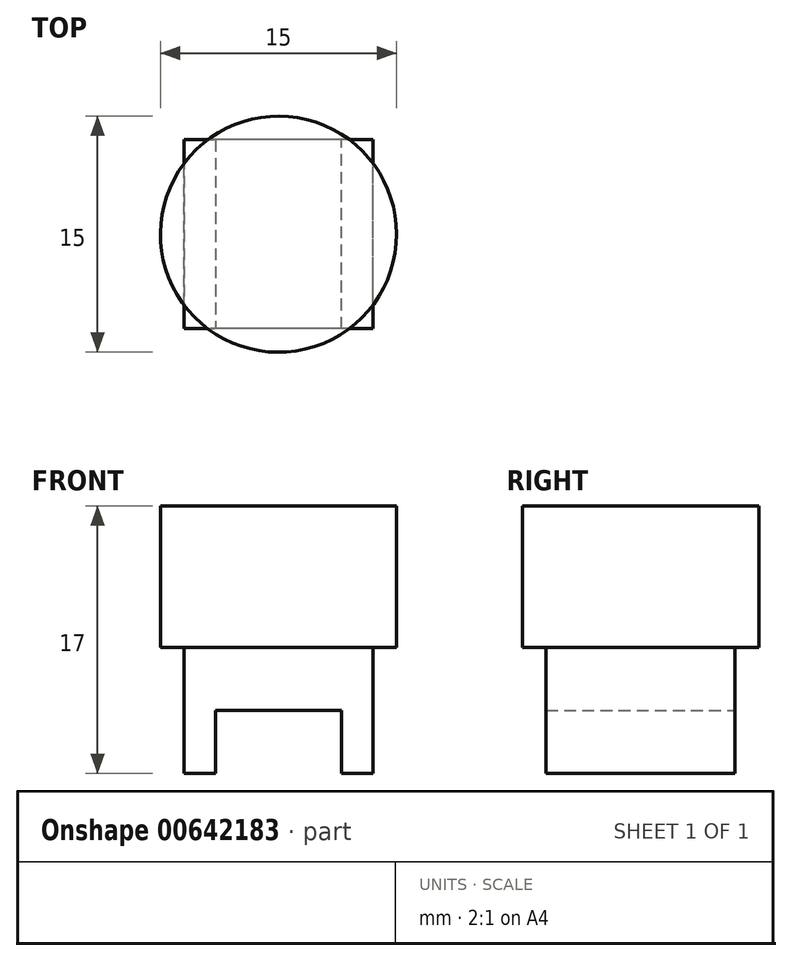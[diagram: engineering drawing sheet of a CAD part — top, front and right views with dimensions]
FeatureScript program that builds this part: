
annotation { "Feature Type Name" : "Feature", "Feature Type Description" : "" }
export const myFeature = defineFeature(function(context is Context, id is Id, definition is map)
    precondition{}
    {
        {
            var Q0;
            Q0=qCreatedBy(makeId("Top.planeOp"),FACE);
            var sketch = newSketch(context, id + "F0", { "sketchPlane" : qUnion([Q0])});
            skLineSegment(sketch, "E0.bottom", {"start": v(6, -6) * mm, "end": v(-6, -6) * mm});
            skLineSegment(sketch, "E0.top", {"start": v(6, 6) * mm, "end": v(-6, 6) * mm});
            skLineSegment(sketch, "E0.left", {"start": v(6, -6) * mm, "end": v(6, 6) * mm});
            skLineSegment(sketch, "E0.right", {"start": v(-6, -6) * mm, "end": v(-6, 6) * mm});
            skPoint(sketch, "E0.middle", {"position": v(0, 0) * mm});
            skSolve(sketch);
        }
        {
            var Q0;
            Q0 = qSketchRegion(id + "F0", true);
            extrude(context, id + "F1", {"entities" : qUnion([Q0]), "oppositeDirection" : true, "depth" : 4 * mm, "offsetDistance" : 25.4 * mm});
        }
        {
            var Q0;
            Q0=qCreatedBy(makeId("Top.planeOp"),FACE);
            var sketch = newSketch(context, id + "F2", { "sketchPlane" : qUnion([Q0])});
            skLineSegment(sketch, "E1.bottom", {"start": v(-6, 6) * mm, "end": v(-4, 6) * mm});
            skLineSegment(sketch, "E1.top", {"start": v(-6, -6) * mm, "end": v(-4, -6) * mm});
            skLineSegment(sketch, "E1.left", {"start": v(-6, 6) * mm, "end": v(-6, -6) * mm});
            skLineSegment(sketch, "E1.right", {"start": v(-4, 6) * mm, "end": v(-4, -6) * mm});
            skLineSegment(sketch, "E2.bottom", {"start": v(6, -6) * mm, "end": v(4, -6) * mm});
            skLineSegment(sketch, "E2.top", {"start": v(6, 6) * mm, "end": v(4, 6) * mm});
            skLineSegment(sketch, "E2.left", {"start": v(6, -6) * mm, "end": v(6, 6) * mm});
            skLineSegment(sketch, "E2.right", {"start": v(4, -6) * mm, "end": v(4, 6) * mm});
            skSolve(sketch);
        }
        {
            var Q0;
            Q0 = qSketchRegion(id + "F2", true);
            extrude(context, id + "F3", {"entities" : qUnion([Q0]), "operationType" : NewBodyOperationType.ADD, "oppositeDirection" : true, "depth" : 8 * mm, "offsetDistance" : 25.4 * mm});
        }
        {
            var Q0;
            Q0=qCreatedBy(makeId("Top.planeOp"),FACE);
            var sketch = newSketch(context, id + "F4", { "sketchPlane" : qUnion([Q0])});
            skCircle(sketch, "E3", {"center": v(0, 0) * mm, "radius": 7.5 * mm});
            skSolve(sketch);
        }
        {
            var Q0;
            Q0 = qSketchRegion(id + "F4", true);
            extrude(context, id + "F5", {"entities" : qUnion([Q0]), "operationType" : NewBodyOperationType.ADD, "depth" : 9 * mm, "offsetDistance" : 25.4 * mm});
        }
    });
